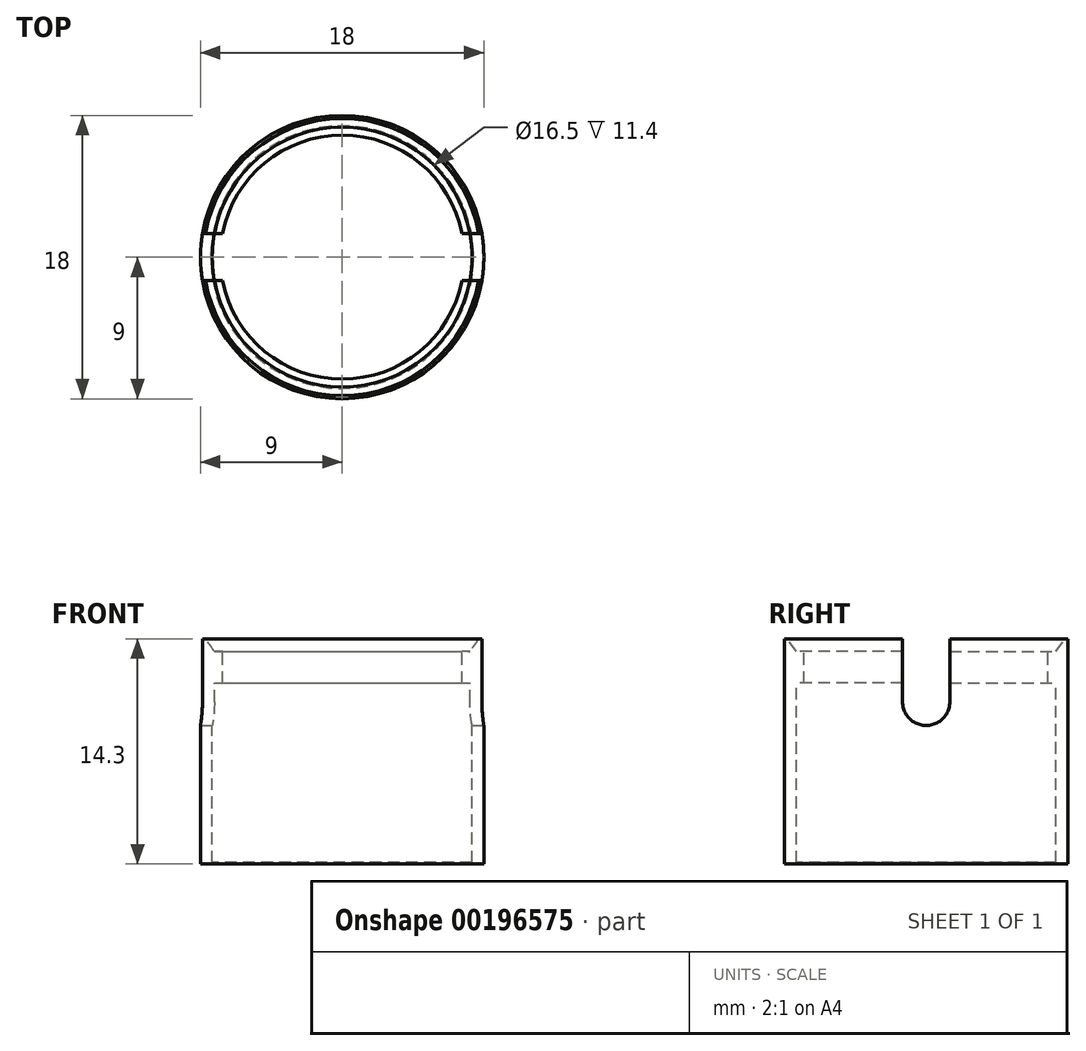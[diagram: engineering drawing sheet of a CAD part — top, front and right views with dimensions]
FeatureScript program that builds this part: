
annotation { "Feature Type Name" : "Feature", "Feature Type Description" : "" }
export const myFeature = defineFeature(function(context is Context, id is Id, definition is map)
    precondition{}
    {
        {
            var Q0;
            Q0=qCreatedBy(makeId("Front.planeOp"),FACE);
            var sketch = newSketch(context, id + "F0", { "sketchPlane" : qUnion([Q0])});
            skLineSegment(sketch, "E0", {"start": v(8.25, 0.1) * mm, "end": v(8.25, 11.5) * mm});
            skLineSegment(sketch, "E1", {"start": v(8.25, 11.5) * mm, "end": v(7.75, 11.5) * mm});
            skLineSegment(sketch, "E2", {"start": v(7.75, 11.5) * mm, "end": v(7.75, 13.5) * mm});
            skLineSegment(sketch, "E3", {"start": v(8.8, 14.3) * mm, "end": v(9, 14.3) * mm});
            skLineSegment(sketch, "E4", {"start": v(9, 14.3) * mm, "end": v(9, 0) * mm});
            skLineSegment(sketch, "E5", {"start": v(9, 0) * mm, "end": v(8.35, 0) * mm});
            skLineSegment(sketch, "E6", {"start": v(0, 14.3) * mm, "end": v(0, 0) * mm, "construction": true});
            skLineSegment(sketch, "E7", {"start": v(7.75, 13.5) * mm, "end": v(8.25, 13.5) * mm});
            skLineSegment(sketch, "E8", {"start": v(8.25, 13.5) * mm, "end": v(8.8, 14.3) * mm});
            skLineSegment(sketch, "E9", {"start": v(8.35, 0) * mm, "end": v(8.25, 0.1) * mm});
            skPoint(sketch, "E10.orphan", {"position": v(8.25, 0) * mm});
            skSolve(sketch);
        }
        {
            var Q0;
            Q0 = qSketchRegion(id + "F0", true);
            var Q1;
            Q1=sQuery(id+"F0.wireOp",EDGE,"E6");
            revolve(context, id + "F1", {"entities" : qUnion([Q0]), "axis" : qUnion([Q1]), "revolveType" : RevolveType.FULL});
        }
        {
            var Q0;
            Q0=qCreatedBy(makeId("Right.planeOp"),FACE);
            var sketch = newSketch(context, id + "F2", { "sketchPlane" : qUnion([Q0])});
            skLineSegment(sketch, "E11", {"start": v(-1.5, 10.3) * mm, "end": v(-1.5, 14.3) * mm});
            skLineSegment(sketch, "E12", {"start": v(-1.5, 14.3) * mm, "end": v(1.5, 14.3) * mm});
            skLineSegment(sketch, "E13", {"start": v(1.5, 14.3) * mm, "end": v(1.5, 10.3) * mm});
            skArc(sketch, "E14", {"start": v(-1.5, 10.3) * mm, "mid": v(0, 8.8) * mm, "end": v(1.5, 10.3) * mm});
            skSolve(sketch);
        }
        {
            var Q0;
            Q0 = qSketchRegion(id + "F2", true);
            extrude(context, id + "F3", {"entities" : qUnion([Q0]), "operationType" : NewBodyOperationType.REMOVE, "endBound" : BoundingType.THROUGH_ALL, "oppositeDirection" : true, "depth" : 25 * mm, "hasSecondDirection" : true, "secondDirectionOppositeDirection" : false, "secondDirectionDepth" : 25 * mm});
        }
    });
